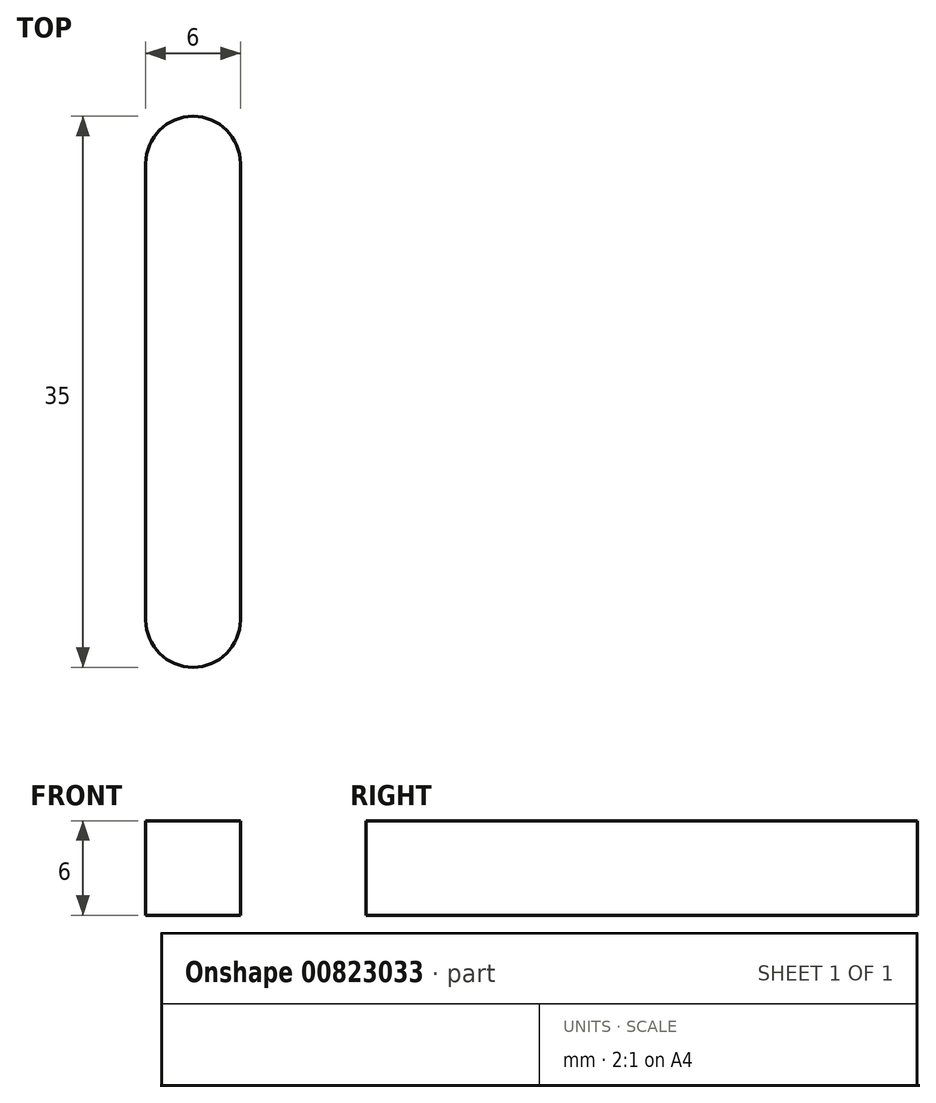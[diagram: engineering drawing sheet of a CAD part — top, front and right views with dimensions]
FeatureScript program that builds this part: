
annotation { "Feature Type Name" : "Feature", "Feature Type Description" : "" }
export const myFeature = defineFeature(function(context is Context, id is Id, definition is map)
    precondition{}
    {
        {
            var Q0;
            Q0=qCreatedBy(makeId("Top.planeOp"),FACE);
            var sketch = newSketch(context, id + "F0", { "sketchPlane" : qUnion([Q0])});
            skLineSegment(sketch, "E0.left", {"start": v(3, 14.5) * mm, "end": v(3, -14.5) * mm});
            skLineSegment(sketch, "E0.right", {"start": v(-3, 14.5) * mm, "end": v(-3, -14.5) * mm});
            skPoint(sketch, "E0.middle", {"position": v(0, 0) * mm});
            skArc(sketch, "E1", {"start": v(3, 14.5) * mm, "mid": v(0, 17.5) * mm, "end": v(-3, 14.5) * mm});
            skArc(sketch, "E2", {"start": v(-3, -14.5) * mm, "mid": v(0, -17.5) * mm, "end": v(3, -14.5) * mm});
            skSolve(sketch);
        }
        {
            var Q0;
            Q0 = qSketchRegion(id + "F0", true);
            extrude(context, id + "F1", {"entities" : qUnion([Q0]), "depth" : 6 * mm, "offsetDistance" : 25 * mm});
        }
    });
